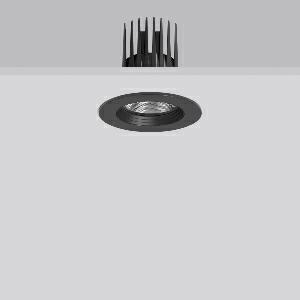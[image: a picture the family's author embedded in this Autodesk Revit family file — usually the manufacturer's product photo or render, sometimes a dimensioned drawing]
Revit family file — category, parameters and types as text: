
# Revit family: heledon_mini_e_901749_003_3_76_4097
name_source: partatom
category: Lighting Fixtures
units: mm (PartAtom-declared; Revit-internal decimal feet)

## family parameters
Cut with Voids When Loaded = No
Host = Face
Light Source = No
Part Type = Normal
Room Calculation Point = No
Round Connector Dimension = Use Diameter
Shared = No

## types (1)
- HELEDON mini E (1 x LED Modul 935, 3600 lm, 3500)
    Apparent Load = 29 VA
    Approval mark = CE
    CIE Flux Codes = 99 100 100 100 100
    Color Rendering = 92
    Color Temperature = 3500
    Default Elevation = 1800 mm
    Description = Series: HELEDON mini
Round recessed downlight. Housing: die-cast aluminium, powder-coated. Black plastic ring and recessed LED to prevent glare from the side. Optical assembly with reflector made of MIRO-Silver with 98% total light reflection for outstanding efficiency - can be changed without tools. Best colour rendering index Ra>90. Suitable for Recessed ceiling mounting. Installation without tools thanks to spring fastening system. Including separate LED converter with connecting cable 600 mm.High quality converter without flickering and stroboscopic effect. Through-wiring box (5 pole) available as accessory. The following accessories can be mounted without use of tools: interchangeable lenses, decorative glasses, honeycomb louvre, clear and frosted diffusers, white interchangeable plastic ring. 
Colour: deep black, matt (RAL 9005)
Diameter: 124 mm
Height: 3 mm
Cut-out diameter: 114 mm
Recess height: 170 mm
Luminaire: recess height: 120 mm
Lamp: LED
Socket: without socket
Colour temperature: 3500K
Colour rendering index (CRI): 92
System power: 29 W
Rated luminous flux: 3600 lm
Luminous efficiency: 124 lm/W
Control gear: Converter, dimmable, DALI
Protection class: II
Type of protection: IP 20
    Height = 0 mm  [stored 0 ft]
    Lamp = 1 x LED Modul 935
    Lamp Light Flux = 3600 lm
    Lamp count = 1
    Length = 124 mm  [stored 0.406824 ft]
    Lifetime = 50000 h
    Luminous efficacy = 124 lm/W
    Manufacturer = RZB
    ModVariant = No
    Model = 901749.003.3.76
    Mounting Place = Ceiling
    Mounting Type = Recessed
    Number of Poles = 1
    OnlyDefault = Yes
    Power Factor = 1
    Product Name = HELEDON mini E
    Product group = Recessed downlights
    ProductGroupID = 402
    Protection Class = Protection class II
    Protection Degree = IP 20
    RLX_Detail_Level = 1
    RLX_Emergency_Light_Flux = 0 lm
    RLX_Emergency_Type = 0
    RLX_Emergency_Type_DB = No
    RlxData = <blob elided: 127433 chars, md5=b8b851fc>
    Socket = socket
    Standby Power = 0 W
    System Light Flux = 3600 lm
    System Power = 29 W
    Type Comments = Product without accessories
    Type Image = 901657.003.jpg
    URL = http://relux.com
    VarID = ---
    Voltage = 230 V
    Voltage Range = 220-240 V
    Weight = 0.00 kg
    Width = 0 mm  [stored 0 ft]

note: [stored X ft] marks values corroborated as IEEE doubles in the binary element streams (Revit-internal decimal feet)

## geometry (parser evidence)
native form markers: Blend x4, Sweep x11
no freeform markers — native parametric forms only
